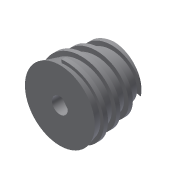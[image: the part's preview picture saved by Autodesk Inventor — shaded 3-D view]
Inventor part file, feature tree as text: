
AUTODESK INVENTOR PART (.ipt)
format: ipt  version: 2019.4 (Build 234330000, 330)  size: 985,088 bytes
history: native  units: mm
features: sketch x6, extrude x3, other x3, revolve x1, sweep x1, reference x1, projected_geometry x1
ambient origin geometry x8: Origin, YZ Plane, XZ Plane, XY Plane, X Axis, Y Axis, Z Axis, Center Point
bodies: Body1 (feature_tree), Body2 (feature_tree), Body3 (feature_tree), Body4 (feature_tree), Body5 (feature_tree), Body6 (feature_tree), Body7 (feature_tree), Body8 (feature_tree), Body9 (feature_tree), Body10 (feature_tree), Body11 (feature_tree), Body12 (feature_tree), Body13 (feature_tree), Body14 (feature_tree), Body15 (feature_tree), Body16 (feature_tree), Body17 (feature_tree), Body18 (feature_tree), Body19 (feature_tree), Body20 (feature_tree), Body21 (feature_tree), Body22 (feature_tree), Body23 (feature_tree), Body24 (feature_tree), Body25 (feature_tree), Body26 (feature_tree), Body27 (feature_tree), Body28 (feature_tree), Body29 (feature_tree), Body30 (feature_tree), Body31 (feature_tree), Body32 (feature_tree), Body33 (feature_tree), Body34 (feature_tree), Body35 (feature_tree), Body36 (feature_tree), Body37 (feature_tree), Body38 (feature_tree), Body39 (feature_tree), Body40 (feature_tree), Body41 (feature_tree), Body42 (feature_tree), Body43 (feature_tree), Body44 (feature_tree), Body45 (feature_tree), Body46 (feature_tree), Body47 (feature_tree), Body48 (feature_tree), Body49 (feature_tree), Body50 (feature_tree), Body51 (feature_tree), Body52 (feature_tree), Body53 (feature_tree), Body54 (feature_tree), Body55 (feature_tree), Body56 (feature_tree), Body57 (feature_tree), Body58 (feature_tree), Body59 (feature_tree), Body60 (feature_tree), Body61 (feature_tree), Body62 (feature_tree), Body63 (feature_tree), Body64 (feature_tree), Body65 (feature_tree), Body66 (feature_tree), Body67 (feature_tree), Body68 (feature_tree), Body69 (feature_tree), Body70 (feature_tree), Body71 (feature_tree), Body72 (feature_tree), Body73 (feature_tree), Body74 (feature_tree), Body75 (feature_tree), Body76 (feature_tree), Body77 (feature_tree), Body78 (feature_tree), Body79 (feature_tree), Body80 (feature_tree), Body81 (feature_tree), Body82 (feature_tree), Body83 (feature_tree), Body84 (feature_tree), Body85 (feature_tree), Body86 (feature_tree), Body87 (feature_tree), Body88 (feature_tree), Body89 (feature_tree), Body90 (feature_tree), Body91 (feature_tree), Body92 (feature_tree), Body93 (feature_tree), Body94 (feature_tree), Body95 (feature_tree), Body96 (feature_tree), Body97 (feature_tree), Body98 (feature_tree), Body99 (feature_tree), Body100 (feature_tree), Body101 (feature_tree), Body102 (feature_tree), Body103 (feature_tree), Body104 (feature_tree), Body105 (feature_tree), Body106 (feature_tree), Body107 (feature_tree), Body108 (feature_tree), Body109 (feature_tree), Body110 (feature_tree), Body111 (feature_tree), Body112 (feature_tree), Body113 (feature_tree), Body114 (feature_tree), Body115 (feature_tree), Body116 (feature_tree), Body117 (feature_tree), Body118 (feature_tree), Body119 (feature_tree), Body120 (feature_tree), Body121 (feature_tree), Body122 (feature_tree), Body123 (feature_tree), Body124 (feature_tree), Body125 (feature_tree), Body126 (feature_tree), Body127 (feature_tree), Body128 (feature_tree), Body129 (feature_tree), Body130 (feature_tree), Body131 (feature_tree), Body132 (feature_tree), Body133 (feature_tree), Body134 (feature_tree), Body135 (feature_tree), Body136 (feature_tree), Body137 (feature_tree), Body138 (feature_tree), Body139 (feature_tree), Body140 (feature_tree), Body141 (feature_tree), Body142 (feature_tree), Body143 (feature_tree), Body144 (feature_tree), Body145 (feature_tree), Body146 (feature_tree), Body147 (feature_tree), Body148 (feature_tree), Body149 (feature_tree), Body150 (feature_tree), Body151 (feature_tree), Body152 (feature_tree), Body153 (feature_tree), Body154 (feature_tree), Body155 (feature_tree), Body156 (feature_tree), Body157 (feature_tree), Body158 (feature_tree), Body159 (feature_tree), Body160 (feature_tree), Body161 (feature_tree), Body162 (feature_tree), Body163 (feature_tree), Body164 (feature_tree), Body165 (feature_tree), Body166 (feature_tree), Body167 (feature_tree), Body168 (feature_tree), Body169 (feature_tree), Body170 (feature_tree), Body171 (feature_tree), Body172 (feature_tree), Body173 (feature_tree), Body174 (feature_tree), Body175 (feature_tree), Body176 (feature_tree), Body177 (feature_tree), Body178 (feature_tree), Body179 (feature_tree), Body180 (feature_tree), Body181 (feature_tree), Body182 (feature_tree), Body183 (feature_tree), Body184 (feature_tree), Body185 (feature_tree), Body186 (feature_tree), Body187 (feature_tree), Body188 (feature_tree), Body189 (feature_tree), Body190 (feature_tree), Body191 (feature_tree), Body192 (feature_tree), Body193 (feature_tree), Body194 (feature_tree), Body195 (feature_tree), Body196 (feature_tree), Body197 (feature_tree), Body198 (feature_tree), Body199 (feature_tree), Body200 (feature_tree), Body201 (feature_tree), Body202 (feature_tree), Body203 (feature_tree), Body204 (feature_tree), Body205 (feature_tree), Body206 (feature_tree), Body207 (feature_tree), Body208 (feature_tree), Body209 (feature_tree), Body210 (feature_tree), Body211 (feature_tree), Body212 (feature_tree), Body213 (feature_tree), Body214 (feature_tree), Body215 (feature_tree), Body216 (feature_tree), Body217 (feature_tree), Body218 (feature_tree), Body219 (feature_tree), Body220 (feature_tree), Body221 (feature_tree), Body222 (feature_tree), Body223 (feature_tree), Body224 (feature_tree), Body225 (feature_tree), Body226 (feature_tree), Body227 (feature_tree), Body228 (feature_tree), Body229 (feature_tree), Body230 (feature_tree), Body231 (feature_tree), Body232 (feature_tree), Body233 (feature_tree), Body234 (feature_tree), Body235 (feature_tree), Body236 (feature_tree), Body237 (feature_tree), Body238 (feature_tree), Body239 (feature_tree), Body240 (feature_tree), Body241 (feature_tree), Body242 (feature_tree), Body243 (feature_tree), Body244 (feature_tree), Body245 (feature_tree), Body246 (feature_tree), Body247 (feature_tree), Body248 (feature_tree), Body249 (feature_tree), Body250 (feature_tree), Body251 (feature_tree), Body252 (feature_tree), Body253 (feature_tree), Body254 (feature_tree), Body255 (feature_tree), Body256 (feature_tree), Body257 (feature_tree), Body258 (feature_tree), Body259 (feature_tree), Body260 (feature_tree), Body261 (feature_tree), Body262 (feature_tree), Body263 (feature_tree), Body264 (feature_tree), Body265 (feature_tree), Body266 (feature_tree), Body267 (feature_tree), Body268 (feature_tree), Body269 (feature_tree), Body270 (feature_tree), Body271 (feature_tree), Body272 (feature_tree), Body273 (feature_tree), Body274 (feature_tree), Body275 (feature_tree), Body276 (feature_tree), Body277 (feature_tree), Body278 (feature_tree), Body279 (feature_tree), Body280 (feature_tree), Body281 (feature_tree), Body282 (feature_tree), Body283 (feature_tree), Body284 (feature_tree), Body285 (feature_tree), Body286 (feature_tree), Body287 (feature_tree), Body288 (feature_tree), Body289 (feature_tree), Body290 (feature_tree), Body291 (feature_tree), Body292 (feature_tree), Body293 (feature_tree), Body294 (feature_tree), Body295 (feature_tree), Body296 (feature_tree), Body297 (feature_tree), Body298 (feature_tree), Body299 (feature_tree), Body300 (feature_tree), Body301 (feature_tree), Body302 (feature_tree), Body303 (feature_tree), Body304 (feature_tree), Body305 (feature_tree), Body306 (feature_tree), Body307 (feature_tree), Body308 (feature_tree), Body309 (feature_tree), Body310 (feature_tree), Body311 (feature_tree), Body312 (feature_tree), Body313 (feature_tree), Body314 (feature_tree), Body315 (feature_tree), Body316 (feature_tree), Body317 (feature_tree), Body318 (feature_tree), Body319 (feature_tree), Body320 (feature_tree), Body321 (feature_tree), Body322 (feature_tree), Body323 (feature_tree), Body324 (feature_tree), Body325 (feature_tree), Body326 (feature_tree), Body327 (feature_tree), Body328 (feature_tree), Body329 (feature_tree), Body330 (feature_tree), Body331 (feature_tree), Body332 (feature_tree), Body333 (feature_tree), Body334 (feature_tree), Body335 (feature_tree), Body336 (feature_tree), Body337 (feature_tree), Body338 (feature_tree), Body339 (feature_tree), Body340 (feature_tree), Body341 (feature_tree), Body342 (feature_tree), Body343 (feature_tree), Body344 (feature_tree), Body345 (feature_tree), Body346 (feature_tree), Body347 (feature_tree), Body348 (feature_tree), Body349 (feature_tree)
feature tree (16):
  revolve  "Revolution1"  Angle=90.0deg
  sweep  "Sweep1"
  extrude  "Extrusion3"  Depth=10.0mm TaperAngle=0.0deg
  extrude  "Extrusion4"  Depth=2.9mm
  extrude  "Extrusion5"  [1 undecoded]
  sketch  "Sketch3"  dims[d7=0.1mm d8=90.0deg]
  reference  "Reference3"
  sketch  "3D Sketch1"
  other  "Helical Curve1"
  sketch  "Sketch5"  dims[d9=5.0mm d10=0.0mm d11=15.569mm d12=5.0mm d13=20.0mm d14=22.981mm d15=0.0mm d16=0.0mm]
  sketch  "Sketch6"  dims[d17=10.0mm d18=0.0mm d19=10.0mm d20=0.0mm]
  sketch  "Sketch7"  dims[d21=2.9mm d22=2.9mm]
  sketch  "Sketch8"  dims[d23=10.0mm d24=0.0mm]
  projected_geometry  "Projected Loop2"
  other  "Assembly_Opentrons_Autofocus_v1.iam"
  other  "08_Opentrons_Autofocus_flexurebaering:1"
note: 1 required parameter value undecoded (feature->parameter linkage not recoverable at this tier; creation-order binding heuristic only, values carry confidence <= 0.55)
